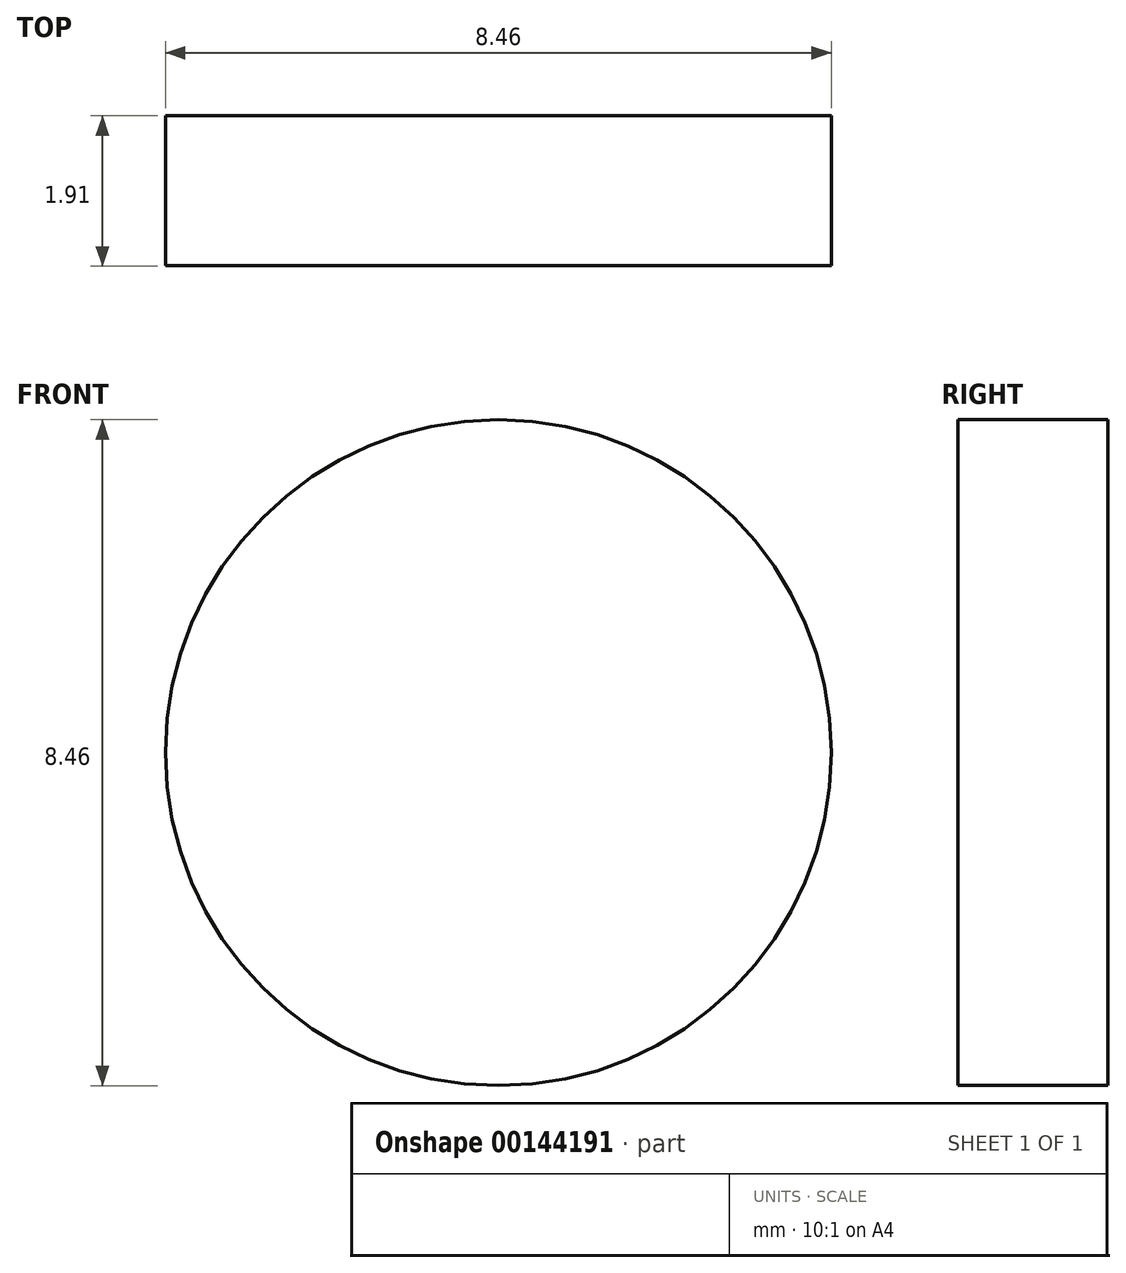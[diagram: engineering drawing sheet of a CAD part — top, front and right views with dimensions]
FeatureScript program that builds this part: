
annotation { "Feature Type Name" : "Feature", "Feature Type Description" : "" }
export const myFeature = defineFeature(function(context is Context, id is Id, definition is map)
    precondition{}
    {
        {
            var Q0;
            Q0=qCreatedBy(makeId("Front.planeOp"),FACE);
            var sketch = newSketch(context, id + "F0", { "sketchPlane" : qUnion([Q0])});
            skCircle(sketch, "E0", {"center": v(0, 0) * mm, "radius": 1.46 * mm});
            skCircle(sketch, "E1", {"center": v(0, 0) * mm, "radius": 4.23 * mm});
            skSolve(sketch);
        }
        {
            var Q0;
            Q0=makeQuery(id+"F0.imprint","IMPRINT",FACE,{"disambiguationData":[TD([[makeQuery(id+"F0.imprint","IMPRINT",EDGE,{"derivedFrom":sQuery(id+"F0.wireOp",EDGE,"E0")}),1.0]])]});
            var Q1;
            Q1=makeQuery(id+"F0.imprint","IMPRINT",FACE,{"disambiguationData":[TD([[makeQuery(id+"F0.imprint","IMPRINT",EDGE,{"derivedFrom":sQuery(id+"F0.wireOp",EDGE,"E0")}),-1.0]])]});
            extrude(context, id + "F1", {"entities" : qUnion([Q0, Q1]), "depth" : 1.9 * mm});
        }
    });
